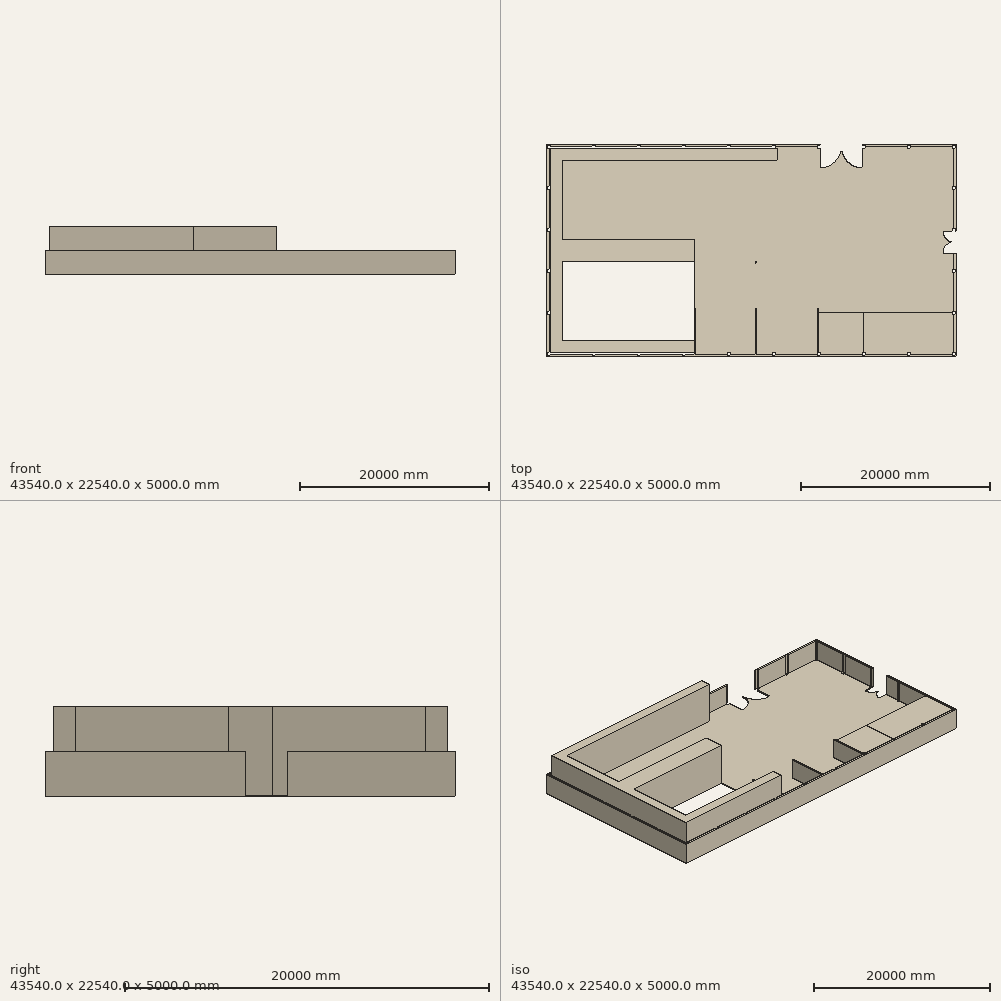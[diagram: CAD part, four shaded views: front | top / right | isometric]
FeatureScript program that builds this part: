
annotation { "Feature Type Name" : "Feature", "Feature Type Description" : "" }
export const myFeature = defineFeature(function(context is Context, id is Id, definition is map)
    precondition{}
    {
        {
            var Q0;
            Q0=qCreatedBy(makeId("Top.planeOp"),FACE);
            var sketch = newSketch(context, id + "F0", { "sketchPlane" : qUnion([Q0])});
            skLineSegment(sketch, "E0", {"start": v(0, 22000) * mm, "end": v(43000, 22000) * mm});
            skLineSegment(sketch, "E1", {"start": v(43000, 22000) * mm, "end": v(43000, 4400) * mm});
            skLineSegment(sketch, "E2", {"start": v(0, 22000) * mm, "end": v(0, 0) * mm});
            skLineSegment(sketch, "E3", {"start": v(0, 0) * mm, "end": v(28666.67, 0) * mm});
            skLineSegment(sketch, "E4.bottom", {"start": v(170, 22170) * mm, "end": v(-170, 22170) * mm});
            skLineSegment(sketch, "E4.top", {"start": v(170, 21830) * mm, "end": v(-170, 21830) * mm});
            skLineSegment(sketch, "E4.left", {"start": v(170, 22170) * mm, "end": v(170, 21830) * mm});
            skLineSegment(sketch, "E4.right", {"start": v(-170, 22170) * mm, "end": v(-170, 21830) * mm});
            skPoint(sketch, "E4.middle", {"position": v(0, 22000) * mm});
            skLineSegment(sketch, "E5.bottom", {"start": v(170, 170) * mm, "end": v(-170, 170) * mm});
            skLineSegment(sketch, "E5.top", {"start": v(170, -170) * mm, "end": v(-170, -170) * mm});
            skLineSegment(sketch, "E5.left", {"start": v(170, 170) * mm, "end": v(170, -170) * mm});
            skLineSegment(sketch, "E5.right", {"start": v(-170, 170) * mm, "end": v(-170, -170) * mm});
            skPoint(sketch, "E5.middle", {"position": v(0, 0) * mm});
            skLineSegment(sketch, "E6.0.1.0", {"start": v(170, 4230) * mm, "end": v(-170, 4230) * mm});
            skLineSegment(sketch, "E6.0.1.1", {"start": v(170, 4570) * mm, "end": v(-170, 4570) * mm});
            skLineSegment(sketch, "E6.0.1.2", {"start": v(170, 4570) * mm, "end": v(170, 4230) * mm});
            skLineSegment(sketch, "E6.0.1.3", {"start": v(-170, 4570) * mm, "end": v(-170, 4230) * mm});
            skLineSegment(sketch, "E6.0.2.0", {"start": v(170, 8630) * mm, "end": v(-170, 8630) * mm});
            skLineSegment(sketch, "E6.0.2.1", {"start": v(170, 8970) * mm, "end": v(-170, 8970) * mm});
            skLineSegment(sketch, "E6.0.2.2", {"start": v(170, 8970) * mm, "end": v(170, 8630) * mm});
            skLineSegment(sketch, "E6.0.2.3", {"start": v(-170, 8970) * mm, "end": v(-170, 8630) * mm});
            skLineSegment(sketch, "E6.0.3.0", {"start": v(170, 13030) * mm, "end": v(-170, 13030) * mm});
            skLineSegment(sketch, "E6.0.3.1", {"start": v(170, 13370) * mm, "end": v(-170, 13370) * mm});
            skLineSegment(sketch, "E6.0.3.2", {"start": v(170, 13370) * mm, "end": v(170, 13030) * mm});
            skLineSegment(sketch, "E6.0.3.3", {"start": v(-170, 13370) * mm, "end": v(-170, 13030) * mm});
            skLineSegment(sketch, "E6.0.4.0", {"start": v(170, 17430) * mm, "end": v(-170, 17430) * mm});
            skLineSegment(sketch, "E6.0.4.1", {"start": v(170, 17770) * mm, "end": v(-170, 17770) * mm});
            skLineSegment(sketch, "E6.0.4.2", {"start": v(170, 17770) * mm, "end": v(170, 17430) * mm});
            skLineSegment(sketch, "E6.0.4.3", {"start": v(-170, 17770) * mm, "end": v(-170, 17430) * mm});
            skLineSegment(sketch, "E7.0.1.0", {"start": v(43170, 4570) * mm, "end": v(43170, 4230) * mm});
            skPoint(sketch, "E7.0.1.1", {"position": v(43000, 4400) * mm});
            skLineSegment(sketch, "E7.0.1.2", {"start": v(42830, 4570) * mm, "end": v(42830, 4230) * mm});
            skLineSegment(sketch, "E7.0.1.4", {"start": v(43170, 4230) * mm, "end": v(42830, 4230) * mm});
            skLineSegment(sketch, "E7.0.1.5", {"start": v(43170, 4570) * mm, "end": v(42830, 4570) * mm});
            skLineSegment(sketch, "E7.0.2.0", {"start": v(43170, 8970) * mm, "end": v(43170, 8630) * mm});
            skPoint(sketch, "E7.0.2.1", {"position": v(43000, 8800) * mm});
            skLineSegment(sketch, "E7.0.2.2", {"start": v(42830, 8970) * mm, "end": v(42830, 8630) * mm});
            skLineSegment(sketch, "E7.0.2.4", {"start": v(43170, 8630) * mm, "end": v(42830, 8630) * mm});
            skLineSegment(sketch, "E7.0.2.5", {"start": v(43170, 8970) * mm, "end": v(42830, 8970) * mm});
            skLineSegment(sketch, "E7.0.3.0", {"start": v(43170, 13370) * mm, "end": v(43170, 13030) * mm});
            skPoint(sketch, "E7.0.3.1", {"position": v(43000, 13200) * mm});
            skLineSegment(sketch, "E7.0.3.2", {"start": v(42830, 13370) * mm, "end": v(42830, 13030) * mm});
            skLineSegment(sketch, "E7.0.3.4", {"start": v(43170, 13030) * mm, "end": v(42830, 13030) * mm});
            skLineSegment(sketch, "E7.0.3.5", {"start": v(43170, 13370) * mm, "end": v(42830, 13370) * mm});
            skLineSegment(sketch, "E7.0.4.0", {"start": v(43170, 17770) * mm, "end": v(43170, 17430) * mm});
            skPoint(sketch, "E7.0.4.1", {"position": v(43000, 17600) * mm});
            skLineSegment(sketch, "E7.0.4.2", {"start": v(42830, 17770) * mm, "end": v(42830, 17430) * mm});
            skLineSegment(sketch, "E7.0.4.4", {"start": v(43170, 17430) * mm, "end": v(42830, 17430) * mm});
            skLineSegment(sketch, "E7.0.4.5", {"start": v(43170, 17770) * mm, "end": v(42830, 17770) * mm});
            skPoint(sketch, "E8.1.0.0", {"position": v(4777.78, 22000) * mm});
            skLineSegment(sketch, "E8.1.0.1", {"start": v(4947.78, 22170) * mm, "end": v(4607.78, 22170) * mm});
            skLineSegment(sketch, "E8.1.0.2", {"start": v(4947.78, 22170) * mm, "end": v(4947.78, 21830) * mm});
            skLineSegment(sketch, "E8.1.0.3", {"start": v(4607.78, 22170) * mm, "end": v(4607.78, 21830) * mm});
            skLineSegment(sketch, "E8.1.0.4", {"start": v(4947.78, 21830) * mm, "end": v(4607.78, 21830) * mm});
            skPoint(sketch, "E8.2.0.0", {"position": v(9555.56, 22000) * mm});
            skLineSegment(sketch, "E8.2.0.1", {"start": v(9725.56, 22170) * mm, "end": v(9385.56, 22170) * mm});
            skLineSegment(sketch, "E8.2.0.2", {"start": v(9725.56, 22170) * mm, "end": v(9725.56, 21830) * mm});
            skLineSegment(sketch, "E8.2.0.3", {"start": v(9385.56, 22170) * mm, "end": v(9385.56, 21830) * mm});
            skLineSegment(sketch, "E8.2.0.4", {"start": v(9725.56, 21830) * mm, "end": v(9385.56, 21830) * mm});
            skPoint(sketch, "E8.3.0.0", {"position": v(14333.33, 22000) * mm});
            skLineSegment(sketch, "E8.3.0.1", {"start": v(14503.33, 22170) * mm, "end": v(14163.33, 22170) * mm});
            skLineSegment(sketch, "E8.3.0.2", {"start": v(14503.33, 22170) * mm, "end": v(14503.33, 21830) * mm});
            skLineSegment(sketch, "E8.3.0.3", {"start": v(14163.33, 22170) * mm, "end": v(14163.33, 21830) * mm});
            skLineSegment(sketch, "E8.3.0.4", {"start": v(14503.33, 21830) * mm, "end": v(14163.33, 21830) * mm});
            skPoint(sketch, "E8.4.0.0", {"position": v(19111.11, 22000) * mm});
            skLineSegment(sketch, "E8.4.0.1", {"start": v(19281.11, 22170) * mm, "end": v(18941.11, 22170) * mm});
            skLineSegment(sketch, "E8.4.0.2", {"start": v(19281.11, 22170) * mm, "end": v(19281.11, 21830) * mm});
            skLineSegment(sketch, "E8.4.0.3", {"start": v(18941.11, 22170) * mm, "end": v(18941.11, 21830) * mm});
            skLineSegment(sketch, "E8.4.0.4", {"start": v(19281.11, 21830) * mm, "end": v(18941.11, 21830) * mm});
            skPoint(sketch, "E8.5.0.0", {"position": v(23888.89, 22000) * mm});
            skLineSegment(sketch, "E8.5.0.1", {"start": v(24058.89, 22170) * mm, "end": v(23718.89, 22170) * mm});
            skLineSegment(sketch, "E8.5.0.2", {"start": v(24058.89, 22170) * mm, "end": v(24058.89, 21830) * mm});
            skLineSegment(sketch, "E8.5.0.3", {"start": v(23718.89, 22170) * mm, "end": v(23718.89, 21830) * mm});
            skLineSegment(sketch, "E8.5.0.4", {"start": v(24058.89, 21830) * mm, "end": v(23718.89, 21830) * mm});
            skPoint(sketch, "E8.6.0.0", {"position": v(28666.67, 22000) * mm});
            skLineSegment(sketch, "E8.6.0.1", {"start": v(28836.67, 22170) * mm, "end": v(28496.67, 22170) * mm});
            skLineSegment(sketch, "E8.6.0.2", {"start": v(28836.67, 22170) * mm, "end": v(28836.67, 21830) * mm});
            skLineSegment(sketch, "E8.6.0.3", {"start": v(28496.67, 22170) * mm, "end": v(28496.67, 21830) * mm});
            skLineSegment(sketch, "E8.6.0.4", {"start": v(28836.67, 21830) * mm, "end": v(28496.67, 21830) * mm});
            skPoint(sketch, "E8.7.0.0", {"position": v(33444.44, 22000) * mm});
            skLineSegment(sketch, "E8.7.0.1", {"start": v(33614.44, 22170) * mm, "end": v(33274.44, 22170) * mm});
            skLineSegment(sketch, "E8.7.0.2", {"start": v(33614.44, 22170) * mm, "end": v(33614.44, 21830) * mm});
            skLineSegment(sketch, "E8.7.0.3", {"start": v(33274.44, 22170) * mm, "end": v(33274.44, 21830) * mm});
            skLineSegment(sketch, "E8.7.0.4", {"start": v(33614.44, 21830) * mm, "end": v(33274.44, 21830) * mm});
            skPoint(sketch, "E8.8.0.0", {"position": v(38222.22, 22000) * mm});
            skLineSegment(sketch, "E8.8.0.1", {"start": v(38392.22, 22170) * mm, "end": v(38052.22, 22170) * mm});
            skLineSegment(sketch, "E8.8.0.2", {"start": v(38392.22, 22170) * mm, "end": v(38392.22, 21830) * mm});
            skLineSegment(sketch, "E8.8.0.3", {"start": v(38052.22, 22170) * mm, "end": v(38052.22, 21830) * mm});
            skLineSegment(sketch, "E8.8.0.4", {"start": v(38392.22, 21830) * mm, "end": v(38052.22, 21830) * mm});
            skPoint(sketch, "E8.9.0.0", {"position": v(43000, 22000) * mm});
            skLineSegment(sketch, "E8.9.0.1", {"start": v(43170, 22170) * mm, "end": v(42830, 22170) * mm});
            skLineSegment(sketch, "E8.9.0.2", {"start": v(43170, 22170) * mm, "end": v(43170, 21830) * mm});
            skLineSegment(sketch, "E8.9.0.3", {"start": v(42830, 22170) * mm, "end": v(42830, 21830) * mm});
            skLineSegment(sketch, "E8.9.0.4", {"start": v(43170, 21830) * mm, "end": v(42830, 21830) * mm});
            skLineSegment(sketch, "E9.1.0.0", {"start": v(4947.78, 170) * mm, "end": v(4607.78, 170) * mm});
            skLineSegment(sketch, "E9.1.0.1", {"start": v(4947.78, -170) * mm, "end": v(4607.78, -170) * mm});
            skPoint(sketch, "E9.1.0.2", {"position": v(4777.78, 0) * mm});
            skLineSegment(sketch, "E9.1.0.3", {"start": v(4607.78, 170) * mm, "end": v(4607.78, -170) * mm});
            skLineSegment(sketch, "E9.1.0.4", {"start": v(4947.78, 170) * mm, "end": v(4947.78, -170) * mm});
            skLineSegment(sketch, "E9.2.0.0", {"start": v(9725.56, 170) * mm, "end": v(9385.56, 170) * mm});
            skLineSegment(sketch, "E9.2.0.1", {"start": v(9725.56, -170) * mm, "end": v(9385.56, -170) * mm});
            skPoint(sketch, "E9.2.0.2", {"position": v(9555.56, 0) * mm});
            skLineSegment(sketch, "E9.2.0.3", {"start": v(9385.56, 170) * mm, "end": v(9385.56, -170) * mm});
            skLineSegment(sketch, "E9.2.0.4", {"start": v(9725.56, 170) * mm, "end": v(9725.56, -170) * mm});
            skLineSegment(sketch, "E9.3.0.0", {"start": v(14503.33, 170) * mm, "end": v(14163.33, 170) * mm});
            skLineSegment(sketch, "E9.3.0.1", {"start": v(14503.33, -170) * mm, "end": v(14163.33, -170) * mm});
            skPoint(sketch, "E9.3.0.2", {"position": v(14333.33, 0) * mm});
            skLineSegment(sketch, "E9.3.0.3", {"start": v(14163.33, 170) * mm, "end": v(14163.33, -170) * mm});
            skLineSegment(sketch, "E9.3.0.4", {"start": v(14503.33, 170) * mm, "end": v(14503.33, -170) * mm});
            skLineSegment(sketch, "E9.4.0.0", {"start": v(19281.11, 170) * mm, "end": v(18941.11, 170) * mm});
            skLineSegment(sketch, "E9.4.0.1", {"start": v(19281.11, -170) * mm, "end": v(18941.11, -170) * mm});
            skPoint(sketch, "E9.4.0.2", {"position": v(19111.11, 0) * mm});
            skLineSegment(sketch, "E9.4.0.3", {"start": v(18941.11, 170) * mm, "end": v(18941.11, -170) * mm});
            skLineSegment(sketch, "E9.4.0.4", {"start": v(19281.11, 170) * mm, "end": v(19281.11, -170) * mm});
            skLineSegment(sketch, "E9.5.0.0", {"start": v(24058.89, 170) * mm, "end": v(23718.89, 170) * mm});
            skLineSegment(sketch, "E9.5.0.1", {"start": v(24058.89, -170) * mm, "end": v(23718.89, -170) * mm});
            skPoint(sketch, "E9.5.0.2", {"position": v(23888.89, 0) * mm});
            skLineSegment(sketch, "E9.5.0.3", {"start": v(23718.89, 170) * mm, "end": v(23718.89, -170) * mm});
            skLineSegment(sketch, "E9.5.0.4", {"start": v(24058.89, 170) * mm, "end": v(24058.89, -170) * mm});
            skLineSegment(sketch, "E9.6.0.0", {"start": v(28836.67, 170) * mm, "end": v(28496.67, 170) * mm});
            skLineSegment(sketch, "E9.6.0.1", {"start": v(28836.67, -170) * mm, "end": v(28496.67, -170) * mm});
            skPoint(sketch, "E9.6.0.2", {"position": v(28666.67, 0) * mm});
            skLineSegment(sketch, "E9.6.0.3", {"start": v(28496.67, 170) * mm, "end": v(28496.67, -170) * mm});
            skLineSegment(sketch, "E9.6.0.4", {"start": v(28836.67, 170) * mm, "end": v(28836.67, -170) * mm});
            skLineSegment(sketch, "E9.7.0.0", {"start": v(33614.44, 170) * mm, "end": v(33274.44, 170) * mm});
            skLineSegment(sketch, "E9.7.0.1", {"start": v(33614.44, -170) * mm, "end": v(33274.44, -170) * mm});
            skPoint(sketch, "E9.7.0.2", {"position": v(33444.44, 0) * mm});
            skLineSegment(sketch, "E9.7.0.3", {"start": v(33274.44, 170) * mm, "end": v(33274.44, -170) * mm});
            skLineSegment(sketch, "E9.7.0.4", {"start": v(33614.44, 170) * mm, "end": v(33614.44, -170) * mm});
            skLineSegment(sketch, "E9.8.0.0", {"start": v(38392.22, 170) * mm, "end": v(38052.22, 170) * mm});
            skLineSegment(sketch, "E9.8.0.1", {"start": v(38392.22, -170) * mm, "end": v(38052.22, -170) * mm});
            skPoint(sketch, "E9.8.0.2", {"position": v(38222.22, 0) * mm});
            skLineSegment(sketch, "E9.8.0.3", {"start": v(38052.22, 170) * mm, "end": v(38052.22, -170) * mm});
            skLineSegment(sketch, "E9.8.0.4", {"start": v(38392.22, 170) * mm, "end": v(38392.22, -170) * mm});
            skLineSegment(sketch, "E9.9.0.0", {"start": v(43170, 170) * mm, "end": v(42830, 170) * mm});
            skLineSegment(sketch, "E9.9.0.1", {"start": v(43170, -170) * mm, "end": v(42830, -170) * mm});
            skPoint(sketch, "E9.9.0.2", {"position": v(43000, 0) * mm});
            skLineSegment(sketch, "E9.9.0.3", {"start": v(42830, 170) * mm, "end": v(42830, -170) * mm});
            skLineSegment(sketch, "E9.9.0.4", {"start": v(43170, 170) * mm, "end": v(43170, -170) * mm});
            skLineSegment(sketch, "E10.bottom", {"start": v(28836.67, 22000) * mm, "end": v(33274.44, 22000) * mm});
            skLineSegment(sketch, "E10.left", {"start": v(28836.67, 22000) * mm, "end": v(28836.67, 19781.11) * mm});
            skLineSegment(sketch, "E10.right", {"start": v(33274.44, 22000) * mm, "end": v(33274.44, 19781.11) * mm});
            skLineSegment(sketch, "E11", {"start": v(28666.67, 0) * mm, "end": v(43000, 0) * mm});
            skLineSegment(sketch, "E12", {"start": v(43000, 4400) * mm, "end": v(43000, 0) * mm});
            skLineSegment(sketch, "E13", {"start": v(43000, 4400) * mm, "end": v(28666.67, 4400) * mm});
            skLineSegment(sketch, "E14", {"start": v(28666.67, 4400) * mm, "end": v(28666.67, 0) * mm});
            skLineSegment(sketch, "E15", {"start": v(33444.44, 0) * mm, "end": v(33444.44, 4400) * mm});
            skLineSegment(sketch, "E16.top", {"start": v(43000, 10730) * mm, "end": v(41850, 10730) * mm});
            skLineSegment(sketch, "E16.left", {"start": v(43000, 13030) * mm, "end": v(43000, 10730) * mm});
            skLineSegment(sketch, "E17.top", {"start": v(69479.6, 14780.56) * mm, "end": v(70779.6, 14780.56) * mm});
            skLineSegment(sketch, "E17.left", {"start": v(69479.6, 17680.56) * mm, "end": v(69479.6, 14780.56) * mm});
            skLineSegment(sketch, "E17.right", {"start": v(70779.6, 17680.56) * mm, "end": v(70779.6, 14780.56) * mm});
            skLineSegment(sketch, "E18", {"start": v(69479.6, 17680.56) * mm, "end": v(69704.6, 17680.56) * mm});
            skLineSegment(sketch, "E19.MirrorCS", {"start": v(69904.6, 17680.56) * mm, "end": v(69904.6, 19280.56) * mm});
            skLineSegment(sketch, "E20", {"start": v(69704.6, 19280.56) * mm, "end": v(69704.6, 17680.56) * mm});
            skLineSegment(sketch, "E21.MirrorCS", {"start": v(70354.6, 17680.56) * mm, "end": v(70354.6, 19280.56) * mm});
            skLineSegment(sketch, "E22.MirrorCS", {"start": v(70554.6, 19280.56) * mm, "end": v(70554.6, 17680.56) * mm});
            skLineSegment(sketch, "E23", {"start": v(69704.6, 19280.56) * mm, "end": v(69904.6, 19280.56) * mm});
            skLineSegment(sketch, "E24.trimOffspring", {"start": v(70354.6, 19280.56) * mm, "end": v(70554.6, 19280.56) * mm});
            skLineSegment(sketch, "E25.bottom", {"start": v(64498.07, 14780.56) * mm, "end": v(65798.07, 14780.56) * mm});
            skLineSegment(sketch, "E25.top", {"start": v(64498.07, 19280.56) * mm, "end": v(65798.07, 19280.56) * mm});
            skLineSegment(sketch, "E25.left", {"start": v(64498.07, 14780.56) * mm, "end": v(64498.07, 19280.56) * mm});
            skLineSegment(sketch, "E25.right", {"start": v(65798.07, 14780.56) * mm, "end": v(65798.07, 19280.56) * mm});
            skLineSegment(sketch, "E26.trimOffspring", {"start": v(69904.6, 17680.56) * mm, "end": v(70354.6, 17680.56) * mm});
            skLineSegment(sketch, "E27.trimOffspring", {"start": v(70554.6, 17680.56) * mm, "end": v(70779.6, 17680.56) * mm});
            skLineSegment(sketch, "E28", {"start": v(30055.67, 19781.11) * mm, "end": v(30055.67, 12220) * mm});
            skLineSegment(sketch, "E29", {"start": v(30055.67, 12220) * mm, "end": v(0, 12220) * mm});
            skLineSegment(sketch, "E30", {"start": v(0, 9780) * mm, "end": v(32055.67, 9780) * mm});
            skLineSegment(sketch, "E31", {"start": v(32055.67, 9780) * mm, "end": v(32055.67, 19781.11) * mm});
            skLineSegment(sketch, "E32", {"start": v(31055.56, 19781.11) * mm, "end": v(31055.56, 11000) * mm, "construction": true});
            skLineSegment(sketch, "E33", {"start": v(31055.56, 11000) * mm, "end": v(0, 11000) * mm, "construction": true});
            skArc(sketch, "E34", {"start": v(43000, 11880) * mm, "mid": v(42186.83, 12216.83) * mm, "end": v(41850, 13030) * mm});
            skLineSegment(sketch, "E35", {"start": v(41850, 13030) * mm, "end": v(43000, 13030) * mm});
            skArc(sketch, "E36", {"start": v(43000, 11880) * mm, "mid": v(42186.83, 11543.17) * mm, "end": v(41850, 10730) * mm});
            skArc(sketch, "E37", {"start": v(31055.56, 22000) * mm, "mid": v(30405.66, 20431) * mm, "end": v(28836.67, 19781.11) * mm});
            skArc(sketch, "E38", {"start": v(31055.56, 22000) * mm, "mid": v(31705.45, 20431) * mm, "end": v(33274.44, 19781.11) * mm});
            skLineSegment(sketch, "E39", {"start": v(28836.67, 19781.11) * mm, "end": v(33274.44, 19781.11) * mm, "construction": true});
            skPoint(sketch, "E40", {"position": v(32055.67, 14780.56) * mm});
            skLineSegment(sketch, "E41.bottom", {"start": v(170, 21830) * mm, "end": v(1390, 21830) * mm});
            skLineSegment(sketch, "E41.top", {"start": v(170, 12730) * mm, "end": v(1390, 12730) * mm});
            skLineSegment(sketch, "E41.left", {"start": v(170, 21830) * mm, "end": v(170, 12730) * mm});
            skLineSegment(sketch, "E41.right", {"start": v(1390, 21830) * mm, "end": v(1390, 12730) * mm});
            skLineSegment(sketch, "E42.bottom", {"start": v(170, 9270) * mm, "end": v(1390, 9270) * mm});
            skLineSegment(sketch, "E42.top", {"start": v(170, 170) * mm, "end": v(1390, 170) * mm});
            skLineSegment(sketch, "E42.left", {"start": v(170, 9270) * mm, "end": v(170, 170) * mm});
            skLineSegment(sketch, "E42.right", {"start": v(1390, 9270) * mm, "end": v(1390, 170) * mm});
            skLineSegment(sketch, "E43.bottom", {"start": v(6590, 170) * mm, "end": v(7810, 170) * mm});
            skLineSegment(sketch, "E43.left", {"start": v(6590, 170) * mm, "end": v(6590, 1390) * mm});
            skLineSegment(sketch, "E43.right", {"start": v(7810, 170) * mm, "end": v(7810, 1390) * mm});
            skLineSegment(sketch, "E44.top", {"start": v(7810, 170) * mm, "end": v(9030, 170) * mm});
            skLineSegment(sketch, "E44.right", {"start": v(9030, 1390) * mm, "end": v(9030, 170) * mm});
            skLineSegment(sketch, "E45", {"start": v(28666.67, 4400) * mm, "end": v(28666.67, 9780) * mm});
            skLineSegment(sketch, "E46.1.0.0", {"start": v(6590, 21830) * mm, "end": v(7810, 21830) * mm});
            skLineSegment(sketch, "E46.1.0.1", {"start": v(7810, 21830) * mm, "end": v(7810, 20610) * mm});
            skLineSegment(sketch, "E46.1.0.3", {"start": v(6590, 21830) * mm, "end": v(6590, 20610) * mm});
            skLineSegment(sketch, "E47.bottom", {"start": v(7810, 21830) * mm, "end": v(9030, 21830) * mm});
            skLineSegment(sketch, "E47.right", {"start": v(9030, 21830) * mm, "end": v(9030, 20610) * mm});
            skLineSegment(sketch, "E48.bottom", {"start": v(1615.09, 17902.8) * mm, "end": v(6115.09, 17902.8) * mm});
            skLineSegment(sketch, "E48.top", {"start": v(1615.09, 16602.8) * mm, "end": v(6115.09, 16602.8) * mm});
            skLineSegment(sketch, "E48.left", {"start": v(1615.09, 17902.8) * mm, "end": v(1615.09, 16602.8) * mm});
            skLineSegment(sketch, "E48.right", {"start": v(6115.09, 17902.8) * mm, "end": v(6115.09, 16602.8) * mm});
            skLineSegment(sketch, "E49.1.0.0", {"start": v(14230, 21830) * mm, "end": v(15450, 21830) * mm});
            skLineSegment(sketch, "E49.1.0.1", {"start": v(15450, 21830) * mm, "end": v(16670, 21830) * mm});
            skLineSegment(sketch, "E49.1.0.2", {"start": v(14230, 21830) * mm, "end": v(14230, 20610) * mm});
            skLineSegment(sketch, "E49.1.0.3", {"start": v(15450, 21830) * mm, "end": v(15450, 20610) * mm});
            skLineSegment(sketch, "E49.1.0.4", {"start": v(16670, 21830) * mm, "end": v(16670, 20610) * mm});
            skLineSegment(sketch, "E49.2.0.0", {"start": v(21870, 21830) * mm, "end": v(23090, 21830) * mm});
            skLineSegment(sketch, "E49.2.0.1", {"start": v(23090, 21830) * mm, "end": v(24310, 21830) * mm});
            skLineSegment(sketch, "E49.2.0.2", {"start": v(21870, 21830) * mm, "end": v(21870, 20610) * mm});
            skLineSegment(sketch, "E49.2.0.3", {"start": v(23090, 21830) * mm, "end": v(23090, 20610) * mm});
            skLineSegment(sketch, "E49.2.0.4", {"start": v(24310, 21830) * mm, "end": v(24310, 20610) * mm});
            skLineSegment(sketch, "E49.direction1", {"start": v(6590, 21830) * mm, "end": v(14230, 21830) * mm, "construction": true});
            skLineSegment(sketch, "E50.1.0.1", {"start": v(14230, 170) * mm, "end": v(14230, 1390) * mm});
            skLineSegment(sketch, "E50.1.0.4", {"start": v(15450, 170) * mm, "end": v(15450, 9270) * mm});
            skLineSegment(sketch, "E50.1.0.6", {"start": v(14230, 170) * mm, "end": v(15450, 170) * mm});
            skLineSegment(sketch, "E50.direction1", {"start": v(6590, 170) * mm, "end": v(14230, 170) * mm, "construction": true});
            skLineSegment(sketch, "E51", {"start": v(15450, 0) * mm, "end": v(15450, 9780) * mm});
            skLineSegment(sketch, "E52", {"start": v(15450, 9780) * mm, "end": v(28666.67, 9780) * mm});
            skLineSegment(sketch, "E53", {"start": v(22058.33, 9780) * mm, "end": v(22058.33, 0) * mm});
            skLineSegment(sketch, "E54.bottom", {"start": v(1390, 21830) * mm, "end": v(6590, 21830) * mm});
            skLineSegment(sketch, "E54.top", {"start": v(1390, 20610) * mm, "end": v(6590, 20610) * mm});
            skLineSegment(sketch, "E54.left", {"start": v(1390, 21830) * mm, "end": v(1390, 20610) * mm});
            skLineSegment(sketch, "E55.bottom", {"start": v(9030, 21830) * mm, "end": v(14230, 21830) * mm});
            skLineSegment(sketch, "E55.top", {"start": v(9030, 20610) * mm, "end": v(14230, 20610) * mm});
            skLineSegment(sketch, "E56.bottom", {"start": v(16670, 21830) * mm, "end": v(21870, 21830) * mm});
            skLineSegment(sketch, "E56.top", {"start": v(16670, 20610) * mm, "end": v(21870, 20610) * mm});
            skLineSegment(sketch, "E57.bottom", {"start": v(1390, 170) * mm, "end": v(6590, 170) * mm});
            skLineSegment(sketch, "E57.top", {"start": v(1390, 1390) * mm, "end": v(6590, 1390) * mm});
            skLineSegment(sketch, "E57.left", {"start": v(1390, 170) * mm, "end": v(1390, 1390) * mm});
            skLineSegment(sketch, "E58.bottom", {"start": v(9030, 170) * mm, "end": v(14230, 170) * mm});
            skLineSegment(sketch, "E58.top", {"start": v(9030, 1390) * mm, "end": v(14230, 1390) * mm});
            skLineSegment(sketch, "E58.left", {"start": v(9030, 170) * mm, "end": v(9030, 1390) * mm});
            skLineSegment(sketch, "E59.0", {"start": v(28516.67, 4400) * mm, "end": v(28516.67, 0) * mm});
            skLineSegment(sketch, "E59.1", {"start": v(28516.67, 4400) * mm, "end": v(28516.67, 9630) * mm});
            skLineSegment(sketch, "E59.2", {"start": v(15600, 9630) * mm, "end": v(28516.67, 9630) * mm});
            skLineSegment(sketch, "E59.3", {"start": v(15600, 0) * mm, "end": v(15600, 9630) * mm});
            skLineSegment(sketch, "E60.0", {"start": v(21908.33, 9780) * mm, "end": v(21908.33, -220) * mm});
            skLineSegment(sketch, "E61", {"start": v(15600, 9630) * mm, "end": v(15600, 9780) * mm});
            skLineSegment(sketch, "E62", {"start": v(28516.67, 9630) * mm, "end": v(28516.67, 9780) * mm});
            skLineSegment(sketch, "E63.bottom", {"start": v(-270, 22270) * mm, "end": v(43270, 22270) * mm});
            skLineSegment(sketch, "E63.top", {"start": v(-270, -270) * mm, "end": v(43270, -270) * mm});
            skLineSegment(sketch, "E63.left", {"start": v(-270, 22270) * mm, "end": v(-270, -270) * mm});
            skLineSegment(sketch, "E63.right", {"start": v(43270, 22270) * mm, "end": v(43270, -270) * mm});
            skLineSegment(sketch, "E64", {"start": v(33274.44, 22170) * mm, "end": v(33274.44, 22270) * mm});
            skLineSegment(sketch, "E65", {"start": v(28836.67, 22170) * mm, "end": v(28836.67, 22270) * mm});
            skLineSegment(sketch, "E66", {"start": v(43170, 13030) * mm, "end": v(43270, 13030) * mm});
            skLineSegment(sketch, "E67", {"start": v(43000, 10730) * mm, "end": v(43270, 10730) * mm});
            skCircle(sketch, "E68", {"center": v(11620.8, 16888.07) * mm, "radius": 2342 * mm, "construction": true});
            skLineSegment(sketch, "E69", {"start": v(6590, 1390) * mm, "end": v(9030, 1390) * mm});
            skLineSegment(sketch, "E70", {"start": v(14230, 1390) * mm, "end": v(15450, 1390) * mm});
            skLineSegment(sketch, "E71", {"start": v(1390, 12730) * mm, "end": v(1390, 9270) * mm});
            skLineSegment(sketch, "E72", {"start": v(170, 12730) * mm, "end": v(170, 9270) * mm});
            skLineSegment(sketch, "E73", {"start": v(6590, 20610) * mm, "end": v(9030, 20610) * mm});
            skLineSegment(sketch, "E74", {"start": v(14230, 20610) * mm, "end": v(16670, 20610) * mm});
            skLineSegment(sketch, "E75", {"start": v(21870, 20610) * mm, "end": v(24310, 20610) * mm});
            skLineSegment(sketch, "E76", {"start": v(15450, 9780) * mm, "end": v(15450, 12220) * mm});
            skLineSegment(sketch, "E77", {"start": v(15600, 4815) * mm, "end": v(21908.33, 4815) * mm});
            skLineSegment(sketch, "E78", {"start": v(15600, 4815) * mm, "end": v(15450, 4815) * mm});
            skLineSegment(sketch, "E79", {"start": v(21908.33, 4815) * mm, "end": v(22058.33, 4815) * mm});
            skLineSegment(sketch, "E80", {"start": v(22058.33, 4815) * mm, "end": v(28516.67, 4815) * mm});
            skLineSegment(sketch, "E81", {"start": v(28516.67, 4815) * mm, "end": v(28666.67, 4815) * mm});
            skSolve(sketch);
        }
        {
            var Q0;
            {var subQ62=sQuery(id+"F0.wireOp",EDGE,"E7.0.2.2");Q0=makeQuery(id+"F0.imprint","IMPRINT",FACE,{"disambiguationData":[TD([[makeQuery(id+"F0.imprint","IMPRINT",EDGE,{"derivedFrom":subQ62}),-1.0]])]});}
            var Q1;
            Q1=makeQuery(id+"F0.imprint","IMPRINT",FACE,{"disambiguationData":[TD([[makeQuery(id+"F0.imprint","IMPRINT",EDGE,{"derivedFrom":sQuery(id+"F0.wireOp",EDGE,"E48.bottom")}),-1.0]])]});
            var Q2;
            {var subQ7=sQuery(id+"F0.wireOp",EDGE,"E9.6.0.4");var subQ8=sQuery(id+"F0.wireOp",EDGE,"E9.6.0.0");var subQ9=makeQuery(id+"F0.imprint","INTERSECT",VERTEX,{"derivedFrom":[subQ8,subQ7]});Q2=makeQuery(id+"F0.imprint","IMPRINT",FACE,{"disambiguationData":[TD([[makeQuery(id+"F0.imprint","IMPRINT",EDGE,{"disambiguationData":[TD([[subQ9,-1.0]])],"derivedFrom":subQ8}),-1.0]])]});}
            var Q3;
            {var subQ18=sQuery(id+"F0.wireOp",EDGE,"E9.8.0.0");Q3=makeQuery(id+"F0.imprint","IMPRINT",FACE,{"disambiguationData":[TD([[makeQuery(id+"F0.imprint","IMPRINT",EDGE,{"derivedFrom":subQ18}),-1.0]])]});}
            var Q4;
            {var subQ11=sQuery(id+"F0.wireOp",EDGE,"E9.5.0.0");Q4=makeQuery(id+"F0.imprint","IMPRINT",FACE,{"disambiguationData":[TD([[makeQuery(id+"F0.imprint","IMPRINT",EDGE,{"derivedFrom":subQ11}),-1.0]])]});}
            var Q5;
            {var subQ1=sQuery(id+"F0.wireOp",EDGE,"E9.4.0.0");Q5=makeQuery(id+"F0.imprint","IMPRINT",FACE,{"disambiguationData":[TD([[makeQuery(id+"F0.imprint","IMPRINT",EDGE,{"derivedFrom":subQ1}),-1.0]])]});}
            var Q6;
            {var subQ5=sQuery(id+"F0.wireOp",EDGE,"E42.right");Q6=makeQuery(id+"F0.imprint","IMPRINT",FACE,{"disambiguationData":[TD([[makeQuery(id+"F0.imprint","IMPRINT",EDGE,{"derivedFrom":subQ5}),1.0]])]});}
            var Q7;
            {var subQ5=sQuery(id+"F0.wireOp",EDGE,"E77");Q7=makeQuery(id+"F0.imprint","IMPRINT",FACE,{"disambiguationData":[TD([[makeQuery(id+"F0.imprint","IMPRINT",EDGE,{"derivedFrom":subQ5}),1.0]])]});}
            var Q8;
            {var subQ0=sQuery(id+"F0.wireOp",EDGE,"E61");Q8=makeQuery(id+"F0.imprint","IMPRINT",FACE,{"disambiguationData":[TD([[makeQuery(id+"F0.imprint","IMPRINT",EDGE,{"derivedFrom":subQ0}),1.0]])]});}
            var Q9;
            {var subQ3=sQuery(id+"F0.wireOp",EDGE,"E61");Q9=makeQuery(id+"F0.imprint","IMPRINT",FACE,{"disambiguationData":[TD([[makeQuery(id+"F0.imprint","IMPRINT",EDGE,{"derivedFrom":subQ3}),-1.0]])]});}
            var Q10;
            {var subQ0=sQuery(id+"F0.wireOp",EDGE,"E53");var subQ1=sQuery(id+"F0.wireOp",EDGE,"E52");var subQ2=makeQuery(id+"F0.imprint","INTERSECT",VERTEX,{"derivedFrom":[subQ1,subQ0]});Q10=makeQuery(id+"F0.imprint","IMPRINT",FACE,{"disambiguationData":[TD([[makeQuery(id+"F0.imprint","IMPRINT",EDGE,{"disambiguationData":[TD([[subQ2,1.0]])],"derivedFrom":subQ1}),-1.0]])]});}
            var Q11;
            {var subQ0=sQuery(id+"F0.wireOp",EDGE,"E79");Q11=makeQuery(id+"F0.imprint","IMPRINT",FACE,{"disambiguationData":[TD([[makeQuery(id+"F0.imprint","IMPRINT",EDGE,{"derivedFrom":subQ0}),1.0]])]});}
            var Q12;
            {var subQ3=sQuery(id+"F0.wireOp",EDGE,"E62");Q12=makeQuery(id+"F0.imprint","IMPRINT",FACE,{"disambiguationData":[TD([[makeQuery(id+"F0.imprint","IMPRINT",EDGE,{"derivedFrom":subQ3}),1.0]])]});}
            var Q13;
            {var subQ0=sQuery(id+"F0.wireOp",EDGE,"E80");Q13=makeQuery(id+"F0.imprint","IMPRINT",FACE,{"disambiguationData":[TD([[makeQuery(id+"F0.imprint","IMPRINT",EDGE,{"derivedFrom":subQ0}),1.0]])]});}
            var Q14;
            {var subQ0=sQuery(id+"F0.wireOp",EDGE,"E62");Q14=makeQuery(id+"F0.imprint","IMPRINT",FACE,{"disambiguationData":[TD([[makeQuery(id+"F0.imprint","IMPRINT",EDGE,{"derivedFrom":subQ0}),-1.0]])]});}
            extrude(context, id + "F1", {"entities" : qUnion([Q0, Q1, Q2, Q3, Q4, Q5, Q6, Q7, Q8, Q9, Q10, Q11, Q12, Q13, Q14]), "depth" : 100 * mm, "offsetDistance" : 25 * mm});
        }
        {
            var Q0;
            {var subQ3=sQuery(id+"F0.wireOp",EDGE,"E41.bottom");Q0=makeQuery(id+"F0.imprint","IMPRINT",FACE,{"disambiguationData":[TD([[makeQuery(id+"F0.imprint","IMPRINT",EDGE,{"derivedFrom":subQ3}),-1.0]])]});}
            var Q1;
            Q1=makeQuery(id+"F0.imprint","IMPRINT",FACE,{"disambiguationData":[TD([[makeQuery(id+"F0.imprint","IMPRINT",EDGE,{"derivedFrom":sQuery(id+"F0.wireOp",EDGE,"E49.1.0.2")}),1.0]])]});
            var Q2;
            Q2=makeQuery(id+"F0.imprint","IMPRINT",FACE,{"disambiguationData":[TD([[makeQuery(id+"F0.imprint","IMPRINT",EDGE,{"derivedFrom":sQuery(id+"F0.wireOp",EDGE,"E50.1.0.1")}),-1.0]])]});
            var Q3;
            {var subQ3=sQuery(id+"F0.wireOp",EDGE,"E42.bottom");Q3=makeQuery(id+"F0.imprint","IMPRINT",FACE,{"disambiguationData":[TD([[makeQuery(id+"F0.imprint","IMPRINT",EDGE,{"derivedFrom":subQ3}),-1.0]])]});}
            var Q4;
            {var subQ0=sQuery(id+"F0.wireOp",EDGE,"E71");var subQ1=sQuery(id+"F0.wireOp",EDGE,"E29");var subQ2=makeQuery(id+"F0.imprint","INTERSECT",VERTEX,{"derivedFrom":[subQ1,subQ0]});Q4=makeQuery(id+"F0.imprint","IMPRINT",FACE,{"disambiguationData":[TD([[makeQuery(id+"F0.imprint","IMPRINT",EDGE,{"disambiguationData":[TD([[subQ2,-1.0]])],"derivedFrom":subQ1}),1.0]])]});}
            var Q5;
            {var subQ5=sQuery(id+"F0.wireOp",EDGE,"E41.top");Q5=makeQuery(id+"F0.imprint","IMPRINT",FACE,{"disambiguationData":[TD([[makeQuery(id+"F0.imprint","IMPRINT",EDGE,{"derivedFrom":subQ5}),-1.0]])]});}
            var Q6;
            {var subQ5=sQuery(id+"F0.wireOp",EDGE,"E42.bottom");Q6=makeQuery(id+"F0.imprint","IMPRINT",FACE,{"disambiguationData":[TD([[makeQuery(id+"F0.imprint","IMPRINT",EDGE,{"derivedFrom":subQ5}),1.0]])]});}
            var Q7;
            Q7=makeQuery(id+"F0.imprint","IMPRINT",FACE,{"disambiguationData":[TD([[makeQuery(id+"F0.imprint","IMPRINT",EDGE,{"derivedFrom":sQuery(id+"F0.wireOp",EDGE,"E54.top")}),1.0]])]});
            var Q8;
            Q8=makeQuery(id+"F0.imprint","IMPRINT",FACE,{"disambiguationData":[TD([[makeQuery(id+"F0.imprint","IMPRINT",EDGE,{"derivedFrom":sQuery(id+"F0.wireOp",EDGE,"E46.1.0.0")}),-1.0]])]});
            var Q9;
            {var subQ0=sQuery(id+"F0.wireOp",EDGE,"E46.1.0.1");Q9=makeQuery(id+"F0.imprint","IMPRINT",FACE,{"disambiguationData":[TD([[makeQuery(id+"F0.imprint","IMPRINT",EDGE,{"derivedFrom":subQ0}),1.0]])]});}
            var Q10;
            Q10=makeQuery(id+"F0.imprint","IMPRINT",FACE,{"disambiguationData":[TD([[makeQuery(id+"F0.imprint","IMPRINT",EDGE,{"derivedFrom":sQuery(id+"F0.wireOp",EDGE,"E55.top")}),1.0]])]});
            var Q11;
            {var subQ0=sQuery(id+"F0.wireOp",EDGE,"E49.1.0.3");Q11=makeQuery(id+"F0.imprint","IMPRINT",FACE,{"disambiguationData":[TD([[makeQuery(id+"F0.imprint","IMPRINT",EDGE,{"derivedFrom":subQ0}),-1.0]])]});}
            var Q12;
            Q12=makeQuery(id+"F0.imprint","IMPRINT",FACE,{"disambiguationData":[TD([[makeQuery(id+"F0.imprint","IMPRINT",EDGE,{"derivedFrom":sQuery(id+"F0.wireOp",EDGE,"E49.1.0.1")}),-1.0]])]});
            var Q13;
            Q13=makeQuery(id+"F0.imprint","IMPRINT",FACE,{"disambiguationData":[TD([[makeQuery(id+"F0.imprint","IMPRINT",EDGE,{"derivedFrom":sQuery(id+"F0.wireOp",EDGE,"E56.top")}),1.0]])]});
            var Q14;
            Q14=makeQuery(id+"F0.imprint","IMPRINT",FACE,{"disambiguationData":[TD([[makeQuery(id+"F0.imprint","IMPRINT",EDGE,{"derivedFrom":sQuery(id+"F0.wireOp",EDGE,"E49.2.0.0")}),-1.0]])]});
            var Q15;
            {var subQ0=sQuery(id+"F0.wireOp",EDGE,"E49.2.0.3");Q15=makeQuery(id+"F0.imprint","IMPRINT",FACE,{"disambiguationData":[TD([[makeQuery(id+"F0.imprint","IMPRINT",EDGE,{"derivedFrom":subQ0}),1.0]])]});}
            var Q16;
            Q16=makeQuery(id+"F0.imprint","IMPRINT",FACE,{"disambiguationData":[TD([[makeQuery(id+"F0.imprint","IMPRINT",EDGE,{"derivedFrom":sQuery(id+"F0.wireOp",EDGE,"E57.top")}),-1.0]])]});
            var Q17;
            Q17=makeQuery(id+"F0.imprint","IMPRINT",FACE,{"disambiguationData":[TD([[makeQuery(id+"F0.imprint","IMPRINT",EDGE,{"derivedFrom":sQuery(id+"F0.wireOp",EDGE,"E43.bottom")}),1.0]])]});
            var Q18;
            {var subQ0=sQuery(id+"F0.wireOp",EDGE,"E43.right");Q18=makeQuery(id+"F0.imprint","IMPRINT",FACE,{"disambiguationData":[TD([[makeQuery(id+"F0.imprint","IMPRINT",EDGE,{"derivedFrom":subQ0}),-1.0]])]});}
            var Q19;
            Q19=makeQuery(id+"F0.imprint","IMPRINT",FACE,{"disambiguationData":[TD([[makeQuery(id+"F0.imprint","IMPRINT",EDGE,{"derivedFrom":sQuery(id+"F0.wireOp",EDGE,"E58.top")}),-1.0]])]});
            var Q20;
            {var subQ0=sQuery(id+"F0.wireOp",EDGE,"E50.1.0.1");Q20=makeQuery(id+"F0.imprint","IMPRINT",FACE,{"disambiguationData":[TD([[makeQuery(id+"F0.imprint","IMPRINT",EDGE,{"derivedFrom":subQ0}),-1.0]])]});}
            var Q21;
            {var subQ0=sQuery(id+"F0.wireOp",EDGE,"E76");Q21=makeQuery(id+"F0.imprint","IMPRINT",FACE,{"disambiguationData":[TD([[makeQuery(id+"F0.imprint","IMPRINT",EDGE,{"derivedFrom":subQ0}),1.0]])]});}
            extrude(context, id + "F2", {"entities" : qUnion([Q0, Q1, Q2, Q3, Q4, Q5, Q6, Q7, Q8, Q9, Q10, Q11, Q12, Q13, Q14, Q15, Q16, Q17, Q18, Q19, Q20, Q21]), "depth" : 5000 * mm, "offsetDistance" : 25 * mm});
        }
        {
            var Q0;
            {var subQ0=sQuery(id+"F0.wireOp",EDGE,"E53");var subQ1=sQuery(id+"F0.wireOp",EDGE,"E3");var subQ2=makeQuery(id+"F0.imprint","INTERSECT",VERTEX,{"derivedFrom":[subQ1,subQ0]});Q0=makeQuery(id+"F0.imprint","IMPRINT",FACE,{"disambiguationData":[TD([[makeQuery(id+"F0.imprint","IMPRINT",EDGE,{"disambiguationData":[TD([[subQ2,1.0]])],"derivedFrom":subQ1}),1.0]])]});}
            var Q1;
            {var subQ2=sQuery(id+"F0.wireOp",EDGE,"E78");Q1=makeQuery(id+"F0.imprint","IMPRINT",FACE,{"disambiguationData":[TD([[makeQuery(id+"F0.imprint","IMPRINT",EDGE,{"derivedFrom":subQ2}),1.0]])]});}
            var Q2;
            {var subQ8=sQuery(id+"F0.wireOp",EDGE,"E81");Q2=makeQuery(id+"F0.imprint","IMPRINT",FACE,{"disambiguationData":[TD([[makeQuery(id+"F0.imprint","IMPRINT",EDGE,{"derivedFrom":subQ8}),-1.0]])]});}
            extrude(context, id + "F3", {"entities" : qUnion([Q0, Q1, Q2]), "operationType" : NewBodyOperationType.ADD, "depth" : 2500 * mm, "offsetDistance" : 25 * mm});
        }
        {
            var Q0;
            {var subQ122=sQuery(id+"F0.wireOp",EDGE,"E4.bottom");Q0=makeQuery(id+"F0.imprint","IMPRINT",FACE,{"disambiguationData":[TD([[makeQuery(id+"F0.imprint","IMPRINT",EDGE,{"derivedFrom":subQ122}),-1.0]])]});}
            var Q1;
            {var subQ14=sQuery(id+"F0.wireOp",EDGE,"E7.0.3.0");Q1=makeQuery(id+"F0.imprint","IMPRINT",FACE,{"disambiguationData":[TD([[makeQuery(id+"F0.imprint","IMPRINT",EDGE,{"derivedFrom":subQ14}),1.0]])]});}
            extrude(context, id + "F4", {"entities" : qUnion([Q0, Q1]), "operationType" : NewBodyOperationType.ADD, "depth" : 2500 * mm, "offsetDistance" : 25 * mm});
        }
        {
            var Q0;
            {var subQ7=sQuery(id+"F0.wireOp",EDGE,"E9.6.0.4");var subQ8=sQuery(id+"F0.wireOp",EDGE,"E9.6.0.0");var subQ9=makeQuery(id+"F0.imprint","INTERSECT",VERTEX,{"derivedFrom":[subQ8,subQ7]});Q0=makeQuery(id+"F0.imprint","IMPRINT",FACE,{"disambiguationData":[TD([[makeQuery(id+"F0.imprint","IMPRINT",EDGE,{"disambiguationData":[TD([[subQ9,-1.0]])],"derivedFrom":subQ8}),-1.0]])]});}
            extrude(context, id + "F5", {"entities" : qUnion([Q0]), "depth" : 2500 * mm, "offsetDistance" : 25 * mm});
        }
        {
            var Q0;
            {var subQ11=sQuery(id+"F0.wireOp",EDGE,"E9.8.0.0");Q0=makeQuery(id+"F0.imprint","IMPRINT",FACE,{"disambiguationData":[TD([[makeQuery(id+"F0.imprint","IMPRINT",EDGE,{"derivedFrom":subQ11}),-1.0]])]});}
            extrude(context, id + "F6", {"entities" : qUnion([Q0]), "depth" : 2500 * mm, "offsetDistance" : 25 * mm});
        }
    });
